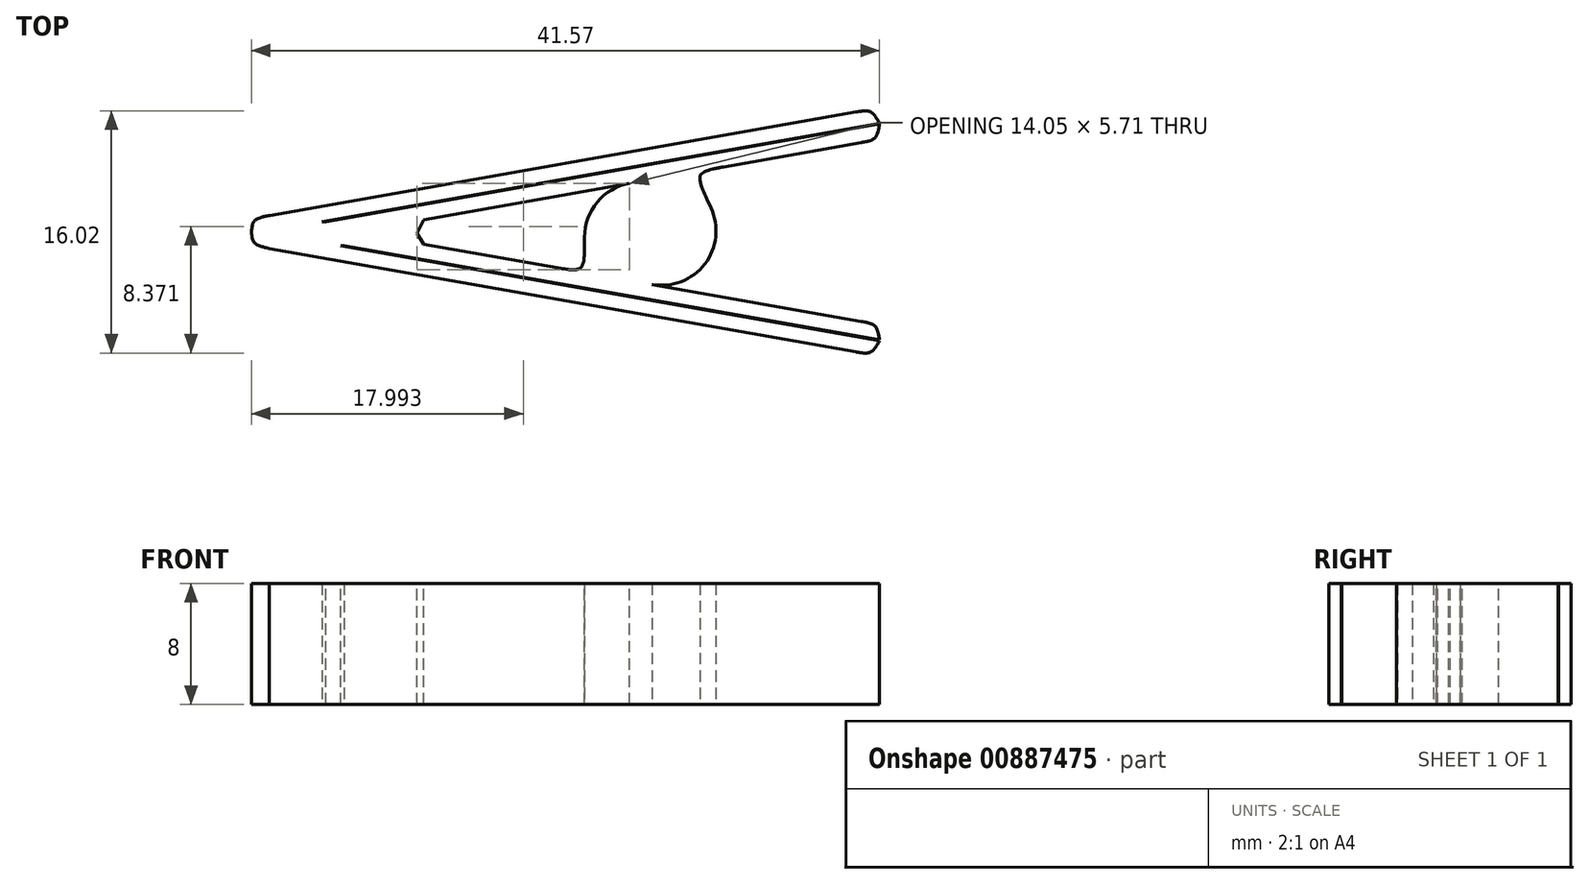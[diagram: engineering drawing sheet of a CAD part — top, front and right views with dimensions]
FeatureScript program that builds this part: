
annotation { "Feature Type Name" : "Feature", "Feature Type Description" : "" }
export const myFeature = defineFeature(function(context is Context, id is Id, definition is map)
    precondition{}
    {
        {
            var Q0;
            Q0=qCreatedBy(makeId("Top.planeOp"),FACE);
            var sketch = newSketch(context, id + "F0", { "sketchPlane" : qUnion([Q0])});
            skCircle(sketch, "E0", {"center": v(1.3, -0.75) * mm, "radius": 1.5 * mm});
            skCircle(sketch, "E1", {"center": v(-1.3, 0.75) * mm, "radius": 1.5 * mm});
            skLineSegment(sketch, "E2", {"start": v(-1.3, 0.75) * mm, "end": v(1.3, -0.75) * mm, "construction": true});
            skLineSegment(sketch, "E3", {"start": v(0, 0) * mm, "end": v(1.93, 0) * mm, "construction": true});
            skSolve(sketch);
        }
        {
            var Q0;
            Q0=qCreatedBy(makeId("Top.planeOp"),FACE);
            var sketch = newSketch(context, id + "F1", { "sketchPlane" : qUnion([Q0])});
            skArc(sketch, "E4", {"start": v(0, 0) * mm, "mid": v(-0.73, 2.14) * mm, "end": v(-2.75, 1.13) * mm});
            skArc(sketch, "E5", {"start": v(0, 0) * mm, "mid": v(0.73, -2.14) * mm, "end": v(2.75, -1.13) * mm});
            skArc(sketch, "E6", {"start": v(2.75, -1.13) * mm, "mid": v(-0.28, 3.37) * mm, "end": v(-4.35, -0.21) * mm});
            skLineSegment(sketch, "E7", {"start": v(-4.35, -0.21) * mm, "end": v(-4.35, -3.34) * mm});
            skLineSegment(sketch, "E8", {"start": v(-1.3, 0.75) * mm, "end": v(-2.05, 2.05) * mm, "construction": true});
            skLineSegment(sketch, "E9", {"start": v(-2.05, 2.05) * mm, "end": v(-2.55, 2.92) * mm, "construction": true});
            skLineSegment(sketch, "E10", {"start": v(1.3, -0.75) * mm, "end": v(1.3, -2.25) * mm, "construction": true});
            skLineSegment(sketch, "E11", {"start": v(1.3, -2.25) * mm, "end": v(1.3, -3.34) * mm, "construction": true});
            skLineSegment(sketch, "E12", {"start": v(0.12, -3.34) * mm, "end": v(-4.35, -3.34) * mm});
            skLineSegment(sketch, "E13", {"start": v(-1.3, 0.75) * mm, "end": v(0.2, 0.75) * mm, "construction": true});
            skLineSegment(sketch, "E14", {"start": v(1.3, -0.75) * mm, "end": v(2.05, -2.05) * mm, "construction": true});
            skLineSegment(sketch, "E15", {"start": v(2.05, -2.05) * mm, "end": v(2.55, -2.92) * mm, "construction": true});
            skArc(sketch, "E16", {"start": v(-2.75, 1.13) * mm, "mid": v(-2.3, -1.73) * mm, "end": v(0.12, -3.34) * mm});
            skLineSegment(sketch, "E17", {"start": v(-0.74, -0.21) * mm, "end": v(0.74, 0.21) * mm, "construction": true});
            skLineSegment(sketch, "E18", {"start": v(0.12, -3.34) * mm, "end": v(-18.85, 0) * mm, "construction": true});
            skLineSegment(sketch, "E19", {"start": v(-18.85, 0) * mm, "end": v(0, 0) * mm, "construction": true});
            skLineSegment(sketch, "E20", {"start": v(-18.85, 0) * mm, "end": v(0.12, 3.34) * mm, "construction": true});
            skSolve(sketch);
        }
        {
            var Q0;
            Q0=makeQuery(id+"F1.imprint","IMPRINT",FACE,{"disambiguationData":[TD([[makeQuery(id+"F1.imprint","IMPRINT",EDGE,{"derivedFrom":sQuery(id+"F1.wireOp",EDGE,"E4")}),-1.0]])]});
            extrude(context, id + "F2", {"entities" : qUnion([Q0]), "endBound" : BoundingType.SYMMETRIC, "depth" : 8 * mm, "offsetDistance" : 25 * mm});
        }
        {
            var Q0;
            Q0=qCreatedBy(makeId("Front.planeOp"),FACE);
            var sketch = newSketch(context, id + "F3", { "sketchPlane" : qUnion([Q0])});
            skLineSegment(sketch, "E21", {"start": v(0, 0) * mm, "end": v(0, 11.64) * mm, "construction": true});
            skSolve(sketch);
        }
        {
            var Q0;
            Q0=makeQuery(id+"F2.opExtrude","SWEPT_BODY",BODY,{"disambiguationData":[OSD([sQuery(id+"F1.wireOp",EDGE,"E4"),sQuery(id+"F1.wireOp",EDGE,"E5"),sQuery(id+"F1.wireOp",EDGE,"E6"),sQuery(id+"F1.wireOp",EDGE,"E7"),sQuery(id+"F1.wireOp",EDGE,"DblR3mlP-tKFU-Pf2z-CLCo-d4s3Zblwjst9"),sQuery(id+"F1.wireOp",EDGE,"E12")])]});
            var Q1;
            Q1=sQuery(id+"F3.wireOp",EDGE,"E21");
            circularPattern(context, id + "F4", {"entities" : qUnion([Q0]), "axis" : qUnion([Q1]), "angle" : 360 * degree, "instanceCount" : 2, "equalSpace" : true});
        }
        {
            var Q0;
            Q0=makeQuery(id+"F2.opExtrude","CAP_FACE",FACE,{"disambiguationData":[OSD([sQuery(id+"F1.wireOp",EDGE,"E4"),sQuery(id+"F1.wireOp",EDGE,"E5"),sQuery(id+"F1.wireOp",EDGE,"E6"),sQuery(id+"F1.wireOp",EDGE,"E7"),sQuery(id+"F1.wireOp",EDGE,"E12"),sQuery(id+"F1.wireOp",EDGE,"E16")])],"isStart":false});
            var sketch = newSketch(context, id + "F5", { "sketchPlane" : qUnion([Q0])});
            skLineSegment(sketch, "E22", {"start": v(0, 0) * mm, "end": v(-26.4, 0) * mm, "construction": true});
            skLineSegment(sketch, "E23", {"start": v(-26.4, 1) * mm, "end": v(-26.4, -0.75) * mm});
            skLineSegment(sketch, "E24", {"start": v(-26.4, -0.75) * mm, "end": v(15, -8.05) * mm});
            skLineSegment(sketch, "E25", {"start": v(15, -8.05) * mm, "end": v(15.17, -7.07) * mm});
            skLineSegment(sketch, "E26", {"start": v(15.36, -6.03) * mm, "end": v(-15, -0.68) * mm});
            skLineSegment(sketch, "E27", {"start": v(15.18, -7.02) * mm, "end": v(-24.11, -0.09) * mm});
            skLineSegment(sketch, "E28", {"start": v(-24.48, -0.07) * mm, "end": v(15.17, -7.07) * mm});
            skLineSegment(sketch, "E29.trimOffspring", {"start": v(15.18, -7.02) * mm, "end": v(15.36, -6.03) * mm});
            skLineSegment(sketch, "E30", {"start": v(-24.11, -0.09) * mm, "end": v(-24.48, -0.07) * mm});
            skLineSegment(sketch, "E31", {"start": v(-15.74, 0.6) * mm, "end": v(-15, -0.68) * mm});
            skLineSegment(sketch, "E32", {"start": v(-26.4, 1) * mm, "end": v(-15.74, 0.6) * mm});
            skSolve(sketch);
        }
        {
            var Q0;
            Q0 = qSketchRegion(id + "F5", true);
            var Q1;
            Q1=makeQuery(id+"F2.opExtrude","CAP_FACE",FACE,{"disambiguationData":[OSD([sQuery(id+"F1.wireOp",EDGE,"E4"),sQuery(id+"F1.wireOp",EDGE,"E5"),sQuery(id+"F1.wireOp",EDGE,"E6"),sQuery(id+"F1.wireOp",EDGE,"E7"),sQuery(id+"F1.wireOp",EDGE,"E12"),sQuery(id+"F1.wireOp",EDGE,"E16")])],"isStart":true});
            extrude(context, id + "F6", {"entities" : qUnion([Q0]), "operationType" : NewBodyOperationType.ADD, "endBound" : BoundingType.UP_TO_SURFACE, "oppositeDirection" : true, "depth" : 25 * mm, "endBoundEntityFace" : qUnion([Q1]), "offsetDistance" : 25 * mm});
        }
        {
            var Q0;
            Q0=makeQuery(id+"F4.opPattern","COPY",FACE,{"derivedFrom":makeQuery(id+"F2.opExtrude","CAP_FACE",FACE,{"disambiguationData":[OSD([sQuery(id+"F1.wireOp",EDGE,"E4"),sQuery(id+"F1.wireOp",EDGE,"E5"),sQuery(id+"F1.wireOp",EDGE,"E6"),sQuery(id+"F1.wireOp",EDGE,"E7"),sQuery(id+"F1.wireOp",EDGE,"E12"),sQuery(id+"F1.wireOp",EDGE,"E16")])],"isStart":false}),"instanceName":"1"});
            var sketch = newSketch(context, id + "F7", { "sketchPlane" : qUnion([Q0])});
            skLineSegment(sketch, "E33", {"start": v(-15, 0.94) * mm, "end": v(-1.37, 3.34) * mm});
            skLineSegment(sketch, "E34", {"start": v(15.36, 6.3) * mm, "end": v(15.18, 7.28) * mm});
            skLineSegment(sketch, "E35", {"start": v(15, 8.31) * mm, "end": v(-26.4, 1.01) * mm});
            skLineSegment(sketch, "E36", {"start": v(-26.4, 1.01) * mm, "end": v(-26.4, -1) * mm});
            skLineSegment(sketch, "E37", {"start": v(-26.4, -1) * mm, "end": v(-15.74, -0.6) * mm});
            skLineSegment(sketch, "E38", {"start": v(-15.74, -0.6) * mm, "end": v(-15, 0.94) * mm});
            skArc(sketch, "E39", {"start": v(2.84, 0.21) * mm, "mid": v(1.41, 2.69) * mm, "end": v(-1.37, 3.34) * mm});
            skArc(sketch, "E40", {"start": v(4.35, 0.21) * mm, "mid": v(4.27, 1) * mm, "end": v(4.02, 1.74) * mm});
            skLineSegment(sketch, "E41", {"start": v(2.92, 4.1) * mm, "end": v(4.02, 1.74) * mm});
            skLineSegment(sketch, "E42", {"start": v(-15.74, -0.6) * mm, "end": v(-15.74, 0) * mm, "construction": true});
            skLineSegment(sketch, "E43", {"start": v(-15.74, 0) * mm, "end": v(-15.74, 0.6) * mm, "construction": true});
            skLineSegment(sketch, "E44", {"start": v(4.35, 0.21) * mm, "end": v(2.84, 0.21) * mm});
            skLineSegment(sketch, "E45.trimOffspring", {"start": v(2.92, 4.1) * mm, "end": v(15.36, 6.3) * mm});
            skLineSegment(sketch, "E46", {"start": v(15.17, 7.33) * mm, "end": v(-24.48, 0.34) * mm});
            skLineSegment(sketch, "E47", {"start": v(-24.11, 0.35) * mm, "end": v(15.18, 7.28) * mm});
            skLineSegment(sketch, "E48.trimOffspring", {"start": v(15.17, 7.33) * mm, "end": v(15, 8.31) * mm});
            skLineSegment(sketch, "E49", {"start": v(-24.48, 0.34) * mm, "end": v(-24.11, 0.35) * mm});
            skSolve(sketch);
        }
        {
            var Q0;
            Q0 = qSketchRegion(id + "F7", true);
            var Q1;
            Q1=makeQuery(id+"F4.opPattern","COPY",FACE,{"derivedFrom":makeQuery(id+"F2.opExtrude","CAP_FACE",FACE,{"disambiguationData":[OSD([sQuery(id+"F1.wireOp",EDGE,"E4"),sQuery(id+"F1.wireOp",EDGE,"E5"),sQuery(id+"F1.wireOp",EDGE,"E6"),sQuery(id+"F1.wireOp",EDGE,"E7"),sQuery(id+"F1.wireOp",EDGE,"E12"),sQuery(id+"F1.wireOp",EDGE,"E16")])],"isStart":true}),"instanceName":"1"});
            extrude(context, id + "F8", {"entities" : qUnion([Q0]), "operationType" : NewBodyOperationType.ADD, "endBound" : BoundingType.UP_TO_SURFACE, "oppositeDirection" : true, "depth" : 25 * mm, "endBoundEntityFace" : qUnion([Q1]), "offsetDistance" : 25 * mm});
        }
        {
            var Q0;
            Q0=makeQuery(id+"F8.boolean.opBoolean","MERGE",FACE,{"derivedFrom":[makeQuery(id+"F4.opPattern","COPY",FACE,{"derivedFrom":makeQuery(id+"F2.opExtrude","CAP_FACE",FACE,{"disambiguationData":[OSD([sQuery(id+"F1.wireOp",EDGE,"E4"),sQuery(id+"F1.wireOp",EDGE,"E5"),sQuery(id+"F1.wireOp",EDGE,"E6"),sQuery(id+"F1.wireOp",EDGE,"E7"),sQuery(id+"F1.wireOp",EDGE,"E12"),sQuery(id+"F1.wireOp",EDGE,"E16")])],"isStart":false}),"instanceName":"1"}),makeQuery(id+"F8.opExtrude","CAP_FACE",FACE,{"disambiguationData":[OSD([sQuery(id+"F7.wireOp",EDGE,"E33"),sQuery(id+"F7.wireOp",EDGE,"E34"),sQuery(id+"F7.wireOp",EDGE,"E35"),sQuery(id+"F7.wireOp",EDGE,"E36"),sQuery(id+"F7.wireOp",EDGE,"E37"),sQuery(id+"F7.wireOp",EDGE,"E38"),sQuery(id+"F7.wireOp",EDGE,"E39"),sQuery(id+"F7.wireOp",EDGE,"E40"),sQuery(id+"F7.wireOp",EDGE,"E41"),sQuery(id+"F7.wireOp",EDGE,"E44"),sQuery(id+"F7.wireOp",EDGE,"E45.trimOffspring"),sQuery(id+"F7.wireOp",EDGE,"E46"),sQuery(id+"F7.wireOp",EDGE,"E47"),sQuery(id+"F7.wireOp",EDGE,"E48.trimOffspring"),sQuery(id+"F7.wireOp",EDGE,"E49")])],"isStart":true})]});
            var sketch = newSketch(context, id + "F9", { "sketchPlane" : qUnion([Q0])});
            skLineSegment(sketch, "E50", {"start": v(3.27, 3.34) * mm, "end": v(4.35, 3.34) * mm});
            skLineSegment(sketch, "E51", {"start": v(4.35, 3.34) * mm, "end": v(4.35, 0.21) * mm});
            skLineSegment(sketch, "E52.0", {"start": v(3.27, 3.34) * mm, "end": v(4.02, 1.74) * mm});
            skArc(sketch, "E52.1", {"start": v(4.35, 0.21) * mm, "mid": v(4.27, 1) * mm, "end": v(4.02, 1.74) * mm});
            skPoint(sketch, "E53.orphan", {"position": v(2.92, 4.1) * mm});
            skSolve(sketch);
        }
        {
            var Q0;
            Q0 = qSketchRegion(id + "F9", true);
            extrude(context, id + "F10", {"entities" : qUnion([Q0]), "operationType" : NewBodyOperationType.REMOVE, "endBound" : BoundingType.UP_TO_NEXT, "oppositeDirection" : true, "depth" : 25 * mm, "offsetDistance" : 25 * mm});
        }
        {
            var Q0;
            Q0=makeQuery(id+"F8.opExtrude","SWEPT_EDGE",EDGE,{"disambiguationData":[OSD([sQuery(id+"F7.wireOp",EDGE,"E37"),sQuery(id+"F7.wireOp",EDGE,"E38")])]});
            var Q1;
            Q1=makeQuery(id+"F8.opExtrude","SWEPT_EDGE",EDGE,{"disambiguationData":[OSD([sQuery(id+"F7.wireOp",EDGE,"E35"),sQuery(id+"F7.wireOp",EDGE,"E36")])]});
            var Q2;
            Q2=makeQuery(id+"F8.opExtrude","SWEPT_EDGE",EDGE,{"disambiguationData":[OSD([sQuery(id+"F7.wireOp",EDGE,"E41"),sQuery(id+"F7.wireOp",EDGE,"E45.trimOffspring")])]});
            var Q3;
            Q3=makeQuery(id+"F8.opExtrude","SWEPT_EDGE",EDGE,{"disambiguationData":[OSD([sQuery(id+"F7.wireOp",EDGE,"E34"),sQuery(id+"F7.wireOp",EDGE,"E45.trimOffspring")])]});
            var Q4;
            Q4=makeQuery(id+"F8.opExtrude","SWEPT_EDGE",EDGE,{"disambiguationData":[OSD([sQuery(id+"F7.wireOp",EDGE,"E35"),sQuery(id+"F7.wireOp",EDGE,"E48.trimOffspring")])]});
            var Q5;
            Q5=makeQuery(id+"F6.opExtrude","SWEPT_EDGE",EDGE,{"disambiguationData":[OSD([sQuery(id+"F5.wireOp",EDGE,"E23"),sQuery(id+"F5.wireOp",EDGE,"E24")])]});
            var Q6;
            Q6=makeQuery(id+"F6.opExtrude","SWEPT_EDGE",EDGE,{"disambiguationData":[OSD([sQuery(id+"F5.wireOp",EDGE,"E31"),sQuery(id+"F5.wireOp",EDGE,"E32")])]});
            var Q7;
            Q7=makeQuery(id+"F6.boolean.opBoolean","INTERSECT",EDGE,{"derivedFrom":[makeQuery(id+"F2.opExtrude","SWEPT_FACE",FACE,{"disambiguationData":[OSD([sQuery(id+"F1.wireOp",EDGE,"E7")])]}),makeQuery(id+"F6.opExtrude","SWEPT_FACE",FACE,{"disambiguationData":[OSD([sQuery(id+"F5.wireOp",EDGE,"E26")])]})]});
            var Q8;
            Q8=makeQuery(id+"F6.opExtrude","SWEPT_EDGE",EDGE,{"disambiguationData":[OSD([sQuery(id+"F5.wireOp",EDGE,"E26"),sQuery(id+"F5.wireOp",EDGE,"E29.trimOffspring")])]});
            var Q9;
            Q9=makeQuery(id+"F6.opExtrude","SWEPT_EDGE",EDGE,{"disambiguationData":[OSD([sQuery(id+"F5.wireOp",EDGE,"E24"),sQuery(id+"F5.wireOp",EDGE,"E25")])]});
            var Q10;
            Q10=makeQuery(id+"F8.opExtrude","SWEPT_EDGE",EDGE,{"disambiguationData":[OSD([sQuery(id+"F7.wireOp",EDGE,"E36"),sQuery(id+"F7.wireOp",EDGE,"E37")])]});
            var Q11;
            Q11=makeQuery(id+"F6.opExtrude","SWEPT_EDGE",EDGE,{"disambiguationData":[OSD([sQuery(id+"F5.wireOp",EDGE,"E23"),sQuery(id+"F5.wireOp",EDGE,"E32")])]});
            fillet(context, id + "F11", {"entities" : qUnion([Q0, Q1, Q2, Q3, Q4, Q5, Q6, Q7, Q8, Q9, Q10, Q11]), "radius" : 1.5 * mm, "tangentPropagation" : true, "rho" : .7, "crossSection" : FilletCrossSection.CONIC, "allowEdgeOverflow" : false});
        }
    });
